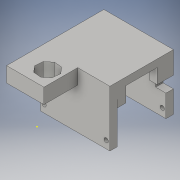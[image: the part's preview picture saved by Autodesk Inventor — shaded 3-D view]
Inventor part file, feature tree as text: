
AUTODESK INVENTOR PART (.ipt)
format: ipt  version: 2016 (Build 200138000, 138)  size: 230,912 bytes
history: native  units: in
note: dims shown in document units (in); Inventor stores cm internally (conversion verified against a paired STEP export)
features: sketch x10, extrude x9
ambient origin geometry x8: Origin, YZ Plane, XZ Plane, XY Plane, X Axis, Y Axis, Z Axis, Center Point
bodies: Solid1 (feature_tree)
feature tree (19):
  extrude  "Extrusion1"  Depth=1.264in
  extrude  "Extrusion2"  Depth=0.25in
  extrude  "Extrusion3"  Depth=2.148in
  extrude  "Extrusion4"  Depth=0.25in
  extrude  "Extrusion5"  Depth=0.25in
  extrude  "Extrusion6"  Depth=1.648in
  extrude  "Extrusion7"  Depth=0.25in
  extrude  "Extrusion8"  Depth=0.25in
  sketch  "Sketch9"  dims[d21=2.355in d22=1.3885in d23=0.0in]
  extrude  "Extrusion9"  Depth=1.3885in TaperAngle=0.0deg
  sketch  "Sketch1"  dims[d0=1.1438in d1=1.264in]
  sketch  "Sketch2"  dims[d5=0.65in d6=0.25in]
  sketch  "Sketch3"  dims[d8=2.3545in d9=2.148in]
  sketch  "Sketch4"  dims[d10=2.3545in d11=0.25in]
  sketch  "Sketch5"  dims[d12=0.5in d13=0.25in]
  sketch  "Sketch6"  dims[d14=1.8545in d15=1.648in]
  sketch  "Sketch7"  dims[d16=0.25in d17=0.25in]
  sketch  "Sketch8"  dims[d18=0.5115in d19=0.0in d20=0.25in]
  sketch  "Sketch10"  dims[d24=0.5115in d25=0.0in d26=2.355in d27=0.5115in d28=1.9in d29=0.0in d30=1.3885in d31=0.0in d37=0.25in d38=0.0in d39=0.35in d40=0.75in d41=0.75in d42=1.6875in d43=0.0in d44=0.2615in d45=0.0in d52=5.824in d53=0.0in d54=0.133in d55=0.2438in d56=1.131in]
